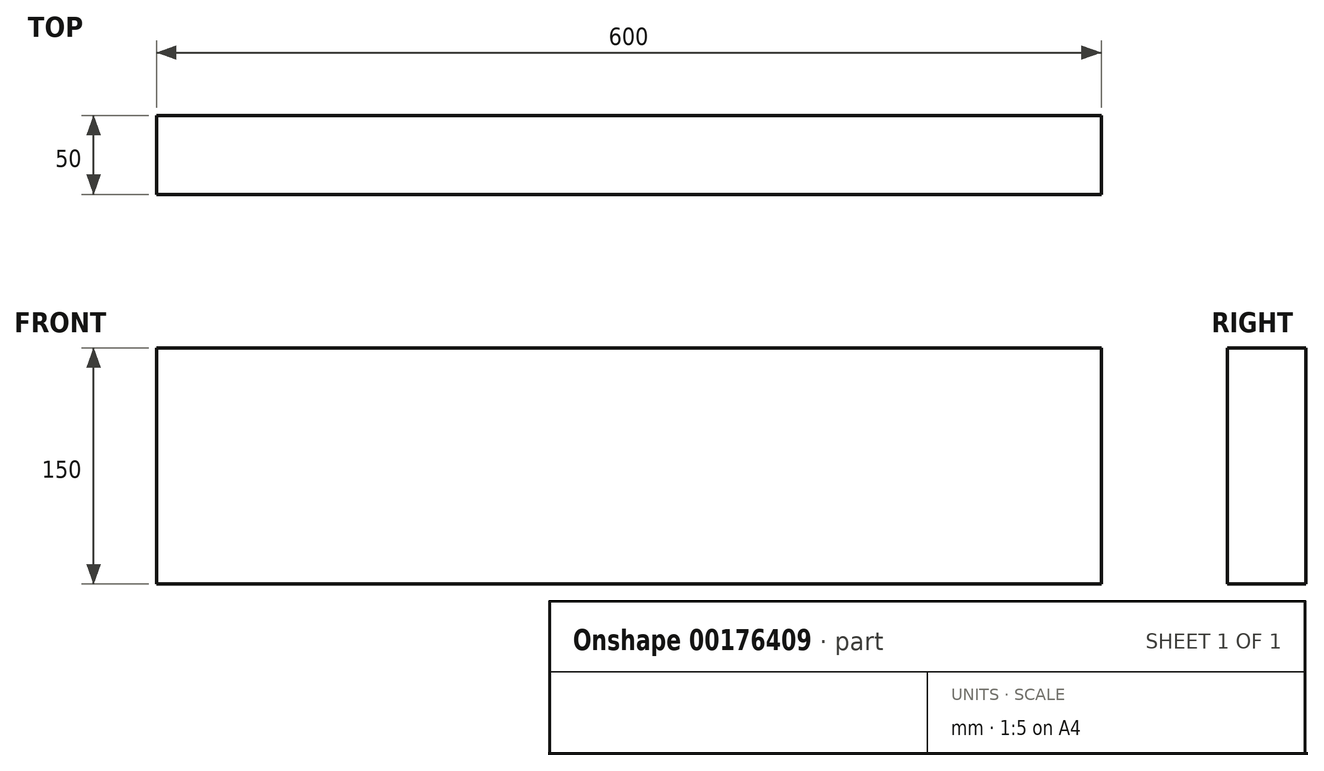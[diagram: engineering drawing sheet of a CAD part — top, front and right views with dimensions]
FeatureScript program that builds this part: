
annotation { "Feature Type Name" : "Feature", "Feature Type Description" : "" }
export const myFeature = defineFeature(function(context is Context, id is Id, definition is map)
    precondition{}
    {
        {
            var Q0;
            Q0=qCreatedBy(makeId("Top.planeOp"),FACE);
            var sketch = newSketch(context, id + "F0", { "sketchPlane" : qUnion([Q0])});
            skLineSegment(sketch, "E0.bottom", {"start": v(300, 25) * mm, "end": v(-300, 25) * mm});
            skLineSegment(sketch, "E0.top", {"start": v(300, -25) * mm, "end": v(-300, -25) * mm});
            skLineSegment(sketch, "E0.left", {"start": v(300, 25) * mm, "end": v(300, -25) * mm});
            skLineSegment(sketch, "E0.right", {"start": v(-300, 25) * mm, "end": v(-300, -25) * mm});
            skPoint(sketch, "E0.middle", {"position": v(0, 0) * mm});
            skSolve(sketch);
        }
        {
            var Q0;
            Q0=makeQuery(id+"F0.imprint","IMPRINT",FACE,{"disambiguationData":[TD([[makeQuery(id+"F0.imprint","IMPRINT",EDGE,{"derivedFrom":sQuery(id+"F0.wireOp",EDGE,"E0.bottom")}),1.0]])]});
            extrude(context, id + "F1", {"entities" : qUnion([Q0]), "depth" : 150 * mm});
        }
    });
